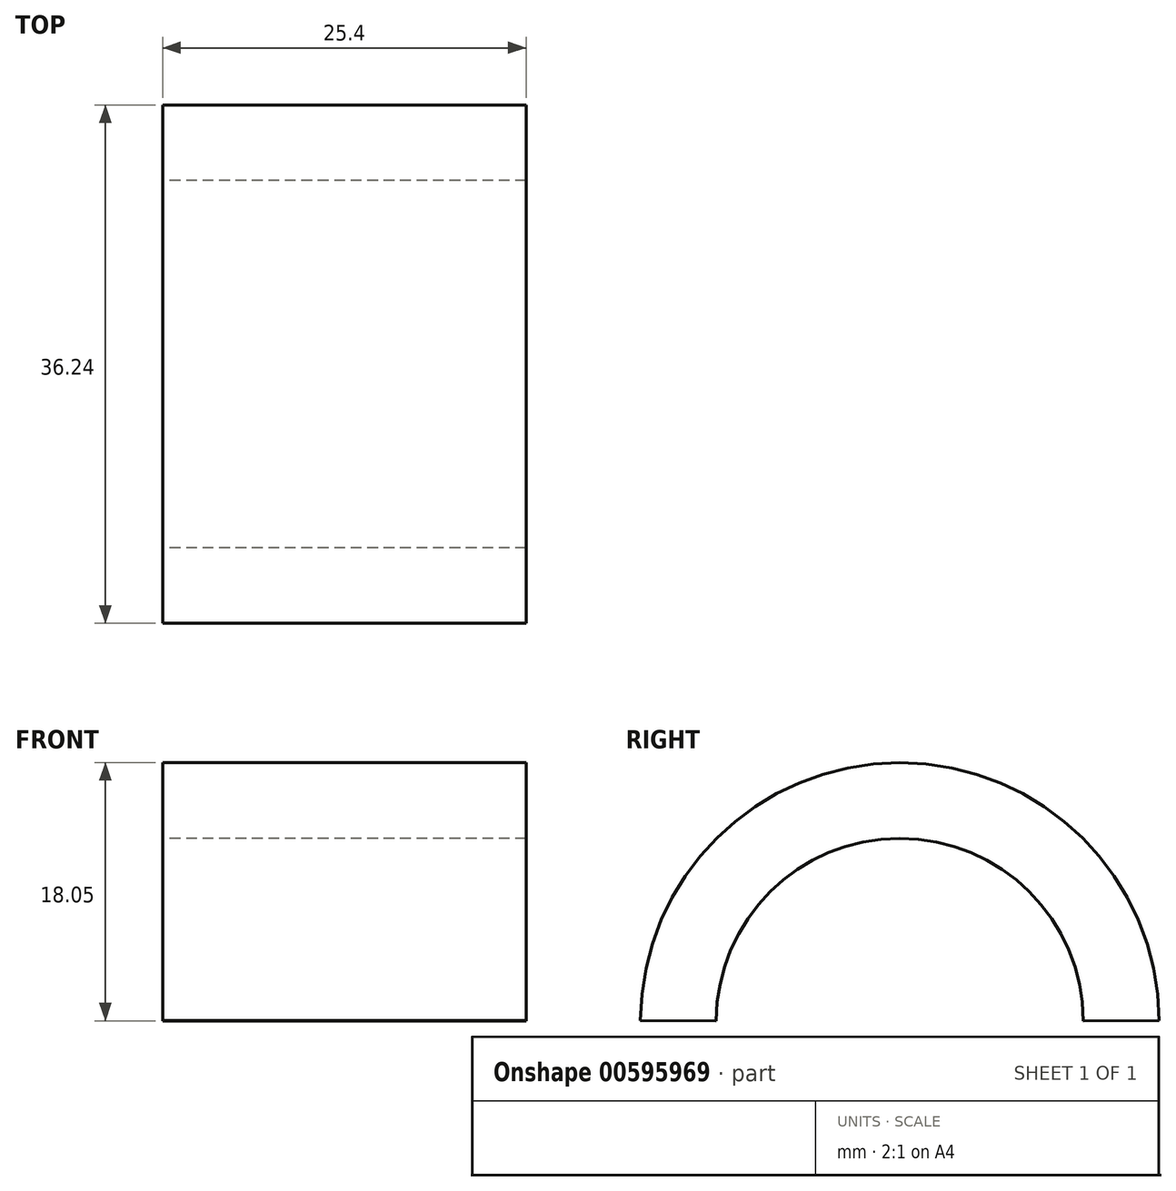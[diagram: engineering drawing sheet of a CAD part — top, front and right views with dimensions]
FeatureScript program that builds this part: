
annotation { "Feature Type Name" : "Feature", "Feature Type Description" : "" }
export const myFeature = defineFeature(function(context is Context, id is Id, definition is map)
    precondition{}
    {
        {
            var Q0;
            Q0=qCreatedBy(makeId("Right.planeOp"),FACE);
            var sketch = newSketch(context, id + "F0", { "sketchPlane" : qUnion([Q0])});
            skArc(sketch, "E0", {"start": v(13.62, 0) * mm, "mid": v(0.8, 12.76) * mm, "end": v(-12.04, 0) * mm});
            skArc(sketch, "E1.0", {"start": v(18.91, 0.03) * mm, "mid": v(0.8, 18.05) * mm, "end": v(-17.33, 0.03) * mm});
            skLineSegment(sketch, "E2", {"start": v(-17.33, 0.03) * mm, "end": v(-12.04, 0) * mm});
            skLineSegment(sketch, "E3", {"start": v(13.62, 0) * mm, "end": v(18.91, 0.03) * mm});
            skSolve(sketch);
        }
        {
            var Q0;
            Q0 = qSketchRegion(id + "F0", true);
            extrude(context, id + "F1", {"entities" : qUnion([Q0]), "depth" : 25.4 * mm, "offsetDistance" : 25.4 * mm});
        }
    });
